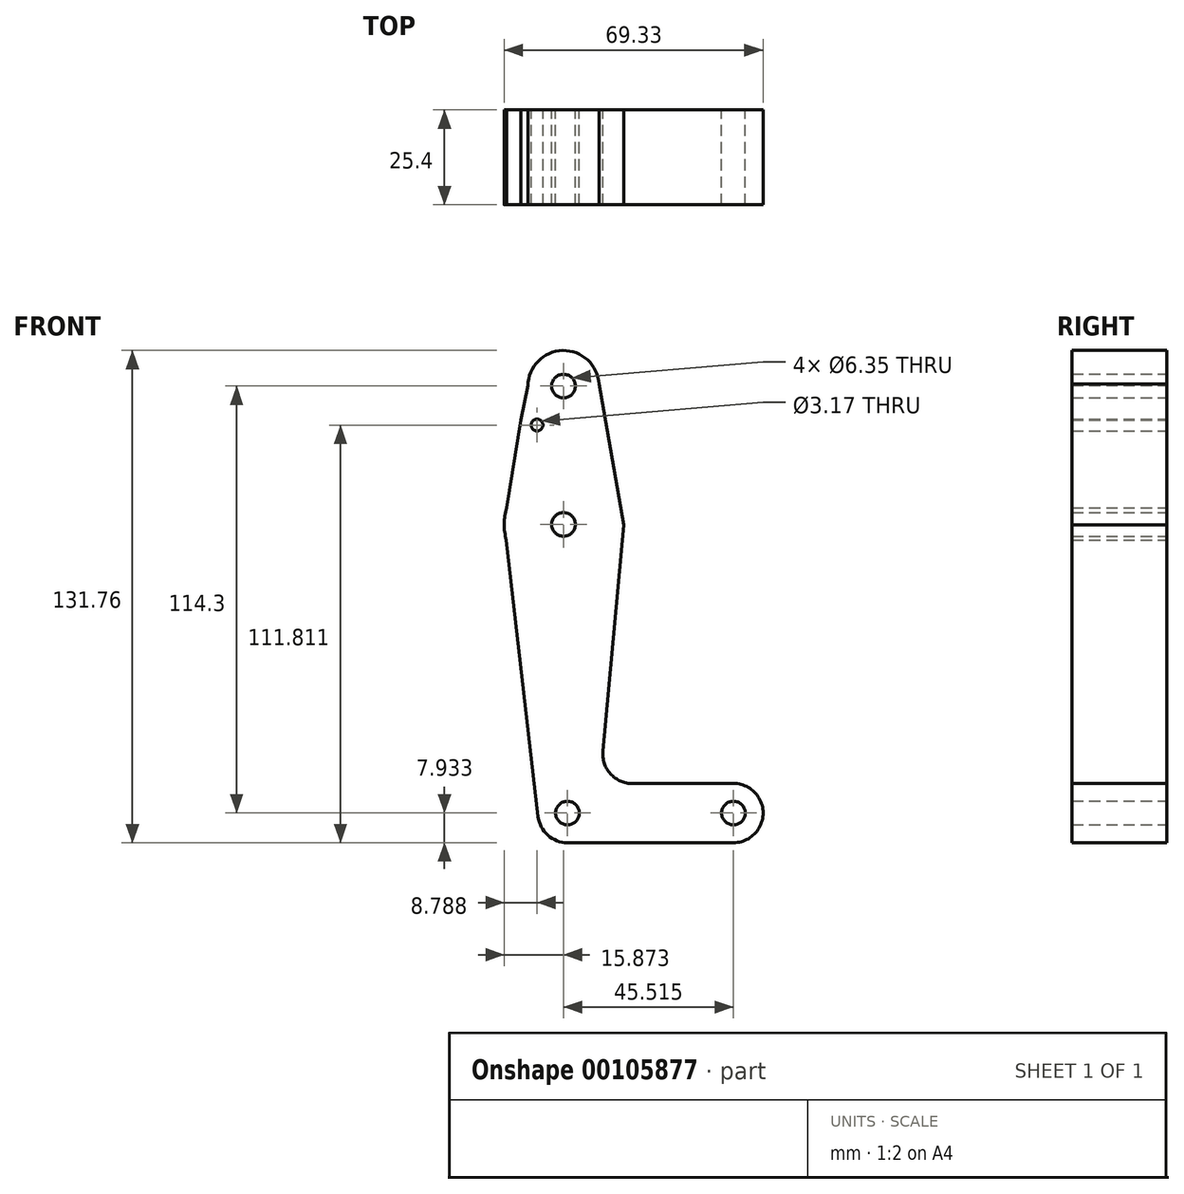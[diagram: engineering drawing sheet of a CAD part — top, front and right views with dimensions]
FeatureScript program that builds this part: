
annotation { "Feature Type Name" : "Feature", "Feature Type Description" : "" }
export const myFeature = defineFeature(function(context is Context, id is Id, definition is map)
    precondition{}
    {
        {
            var Q0;
            Q0=qCreatedBy(makeId("Front.planeOp"),FACE);
            var sketch = newSketch(context, id + "F0", { "sketchPlane" : qUnion([Q0])});
            skLineSegment(sketch, "E0", {"start": v(-35.98, 60.67) * mm, "end": v(-35.98, -53.63) * mm, "construction": true});
            skLineSegment(sketch, "E1", {"start": v(-34.91, -53.63) * mm, "end": v(9.54, -53.63) * mm, "construction": true});
            skCircle(sketch, "E2", {"center": v(-35.98, 60.67) * mm, "radius": 9.53 * mm});
            skCircle(sketch, "E3", {"center": v(-35.98, 23.64) * mm, "radius": 15.88 * mm});
            skCircle(sketch, "E4", {"center": v(-34.91, -53.63) * mm, "radius": 7.94 * mm});
            skCircle(sketch, "E5", {"center": v(9.54, -53.63) * mm, "radius": 7.94 * mm});
            skLineSegment(sketch, "E6", {"start": v(-45.9, 60.8) * mm, "end": v(-51.84, 24.25) * mm});
            skLineSegment(sketch, "E7", {"start": v(-51.84, 24.25) * mm, "end": v(-42.8, -54.53) * mm});
            skLineSegment(sketch, "E8", {"start": v(-26.47, 61.24) * mm, "end": v(-19.83, 23.47) * mm});
            skLineSegment(sketch, "E9", {"start": v(-19.83, 23.47) * mm, "end": v(-25.41, -37.05) * mm});
            skLineSegment(sketch, "E10", {"start": v(-17.48, -45.73) * mm, "end": v(9.53, -45.69) * mm});
            skLineSegment(sketch, "E11", {"start": v(-34.91, -61.56) * mm, "end": v(9.54, -61.56) * mm});
            skCircle(sketch, "E12", {"center": v(-35.98, 60.67) * mm, "radius": 3.18 * mm});
            skCircle(sketch, "E13", {"center": v(-35.98, 23.64) * mm, "radius": 3.18 * mm});
            skCircle(sketch, "E14", {"center": v(-34.91, -53.63) * mm, "radius": 3.18 * mm});
            skCircle(sketch, "E15", {"center": v(9.54, -53.63) * mm, "radius": 3.18 * mm});
            skArc(sketch, "E16.filletArc", {"start": v(-25.41, -37.05) * mm, "mid": v(-23.36, -43.14) * mm, "end": v(-17.48, -45.73) * mm});
            skLineSegment(sketch, "E17", {"start": v(-45.5, 60.8) * mm, "end": v(-47.4, 51.53) * mm});
            skCircle(sketch, "E18", {"center": v(-43.06, 50.25) * mm, "radius": 1.59 * mm});
            skSolve(sketch);
        }
        {
            var Q0;
            Q0 = qSketchRegion(id + "F0", true);
            extrude(context, id + "F1", {"entities" : qUnion([Q0]), "depth" : 25.4 * mm});
        }
    });
